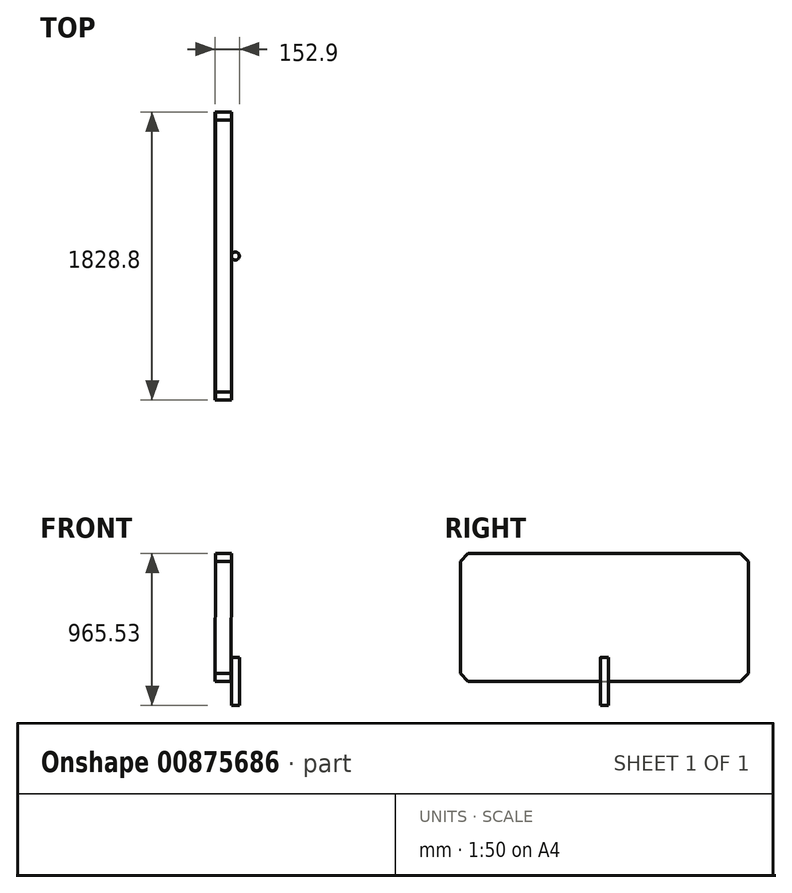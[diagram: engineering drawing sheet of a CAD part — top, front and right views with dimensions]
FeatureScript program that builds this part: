
annotation { "Feature Type Name" : "Feature", "Feature Type Description" : "" }
export const myFeature = defineFeature(function(context is Context, id is Id, definition is map)
    precondition{}
    {
        {
            var Q0;
            Q0=qCreatedBy(makeId("Front.planeOp"),FACE);
            var sketch = newSketch(context, id + "F0", { "sketchPlane" : qUnion([Q0])});
            skLineSegment(sketch, "E0", {"start": v(-102.1, 152.74) * mm, "end": v(-99.41, 965.53) * mm});
            skLineSegment(sketch, "E1", {"start": v(-102.1, 152.74) * mm, "end": v(-0.5, 152.4) * mm});
            skLineSegment(sketch, "E2", {"start": v(-0.5, 152.4) * mm, "end": v(2.19, 965.2) * mm});
            skLineSegment(sketch, "E3", {"start": v(2.19, 965.2) * mm, "end": v(-99.41, 965.53) * mm});
            skLineSegment(sketch, "E4", {"start": v(0, 0) * mm, "end": v(0, 304.8) * mm});
            skLineSegment(sketch, "E5", {"start": v(0, 0) * mm, "end": v(50.8, 0) * mm});
            skLineSegment(sketch, "E6", {"start": v(50.8, 0) * mm, "end": v(50.8, 304.8) * mm});
            skLineSegment(sketch, "E7", {"start": v(50.8, 304.8) * mm, "end": v(0, 304.8) * mm});
            skSolve(sketch);
        }
        {
            var Q0;
            Q0=makeQuery(id+"F0.imprint","IMPRINT",FACE,{"disambiguationData":[TD([[makeQuery(id+"F0.imprint","IMPRINT",EDGE,{"derivedFrom":sQuery(id+"F0.wireOp",EDGE,"E0")}),-1.0]])]});
            extrude(context, id + "F1", {"entities" : qUnion([Q0]), "endBound" : BoundingType.SYMMETRIC, "depth" : 1828.8 * mm, "offsetDistance" : 25.4 * mm});
        }
        {
            var Q0;
            Q0=makeQuery(id+"F1.opExtrude","CAP_EDGE",EDGE,{"disambiguationData":[OSD([sQuery(id+"F0.wireOp",EDGE,"E1")])],"isStart":false});
            var Q1;
            Q1=makeQuery(id+"F1.opExtrude","CAP_EDGE",EDGE,{"disambiguationData":[OSD([sQuery(id+"F0.wireOp",EDGE,"E3")])],"isStart":false});
            var Q2;
            Q2=makeQuery(id+"F1.opExtrude","CAP_EDGE",EDGE,{"disambiguationData":[OSD([sQuery(id+"F0.wireOp",EDGE,"E3")])],"isStart":true});
            var Q3;
            Q3=makeQuery(id+"F1.opExtrude","CAP_EDGE",EDGE,{"disambiguationData":[OSD([sQuery(id+"F0.wireOp",EDGE,"E1")])],"isStart":true});
            chamfer(context, id + "F2", {"entities" : qUnion([Q0, Q1, Q2, Q3]), "width" : 50.8 * mm, "tangentPropagation" : true});
        }
        {
            var Q0;
            Q0=qCreatedBy(makeId("Top.planeOp"),FACE);
            var sketch = newSketch(context, id + "F3", { "sketchPlane" : qUnion([Q0])});
            skCircle(sketch, "E8", {"center": v(25.4, 0) * mm, "radius": 25.4 * mm});
            skSolve(sketch);
        }
        {
            var Q0;
            Q0 = qSketchRegion(id + "F3", true);
            var Q1;
            Q1=sQuery(id+"F0.wireOp",VERTEX,"E4.end");
            extrude(context, id + "F4", {"entities" : qUnion([Q0]), "endBound" : BoundingType.UP_TO_VERTEX, "depth" : 25.4 * mm, "endBoundEntityVertex" : qUnion([Q1]), "offsetDistance" : 25.4 * mm});
        }
    });
